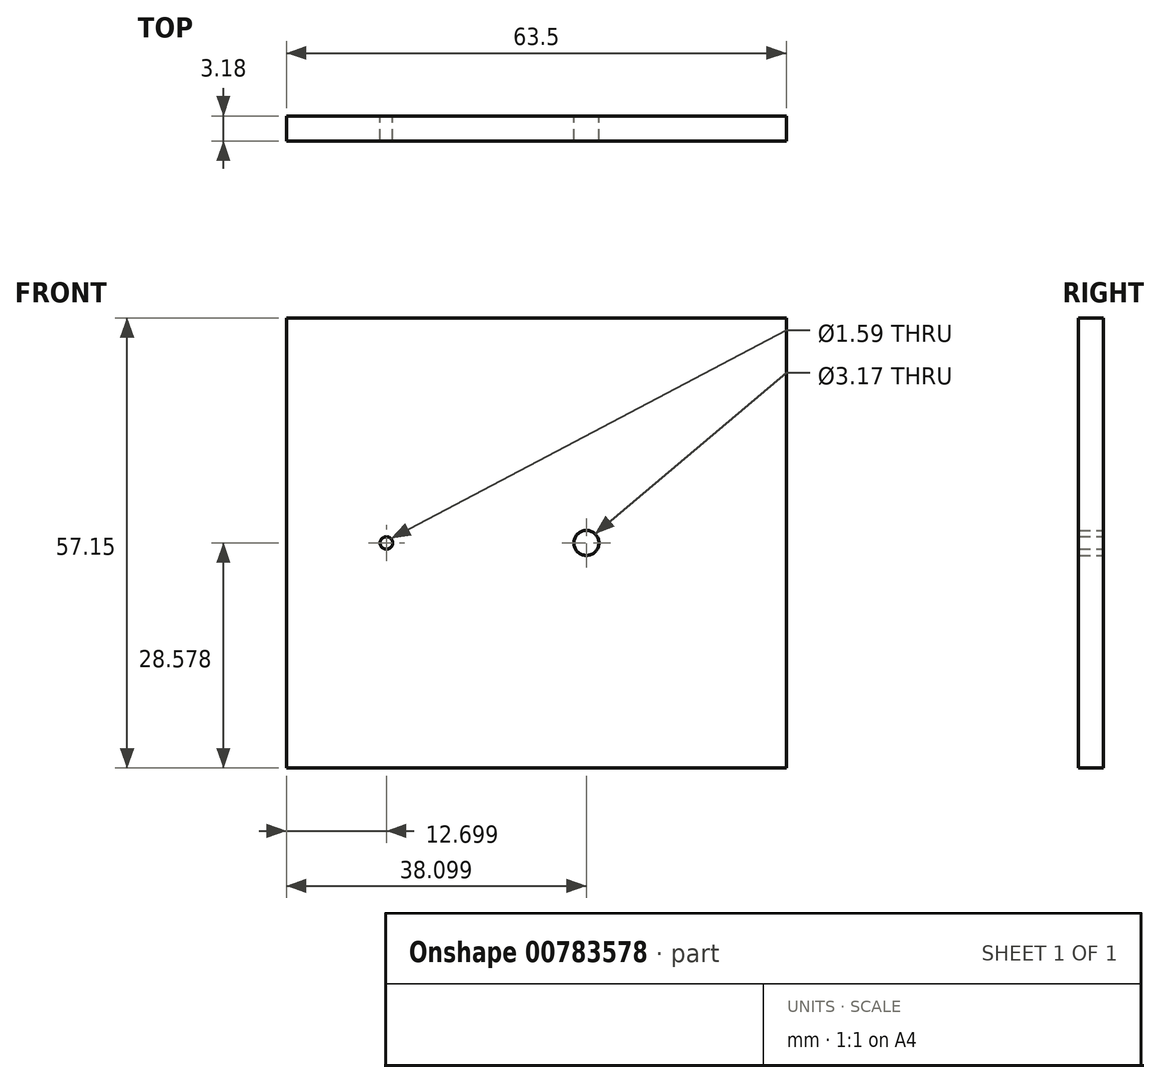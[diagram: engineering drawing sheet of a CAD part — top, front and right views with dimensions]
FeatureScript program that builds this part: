
annotation { "Feature Type Name" : "Feature", "Feature Type Description" : "" }
export const myFeature = defineFeature(function(context is Context, id is Id, definition is map)
    precondition{}
    {
        {
            var Q0;
            Q0=qCreatedBy(makeId("Front.planeOp"),FACE);
            var sketch = newSketch(context, id + "F0", { "sketchPlane" : qUnion([Q0])});
            skLineSegment(sketch, "E0.bottom", {"start": v(6.07, 29.07) * mm, "end": v(-57.43, 29.07) * mm});
            skLineSegment(sketch, "E0.top", {"start": v(6.07, -28.08) * mm, "end": v(-57.43, -28.08) * mm});
            skLineSegment(sketch, "E0.left", {"start": v(6.07, 29.07) * mm, "end": v(6.07, -28.08) * mm});
            skLineSegment(sketch, "E0.right", {"start": v(-57.43, 29.07) * mm, "end": v(-57.43, -28.08) * mm});
            skPoint(sketch, "E1", {"position": v(6.07, 0.5) * mm});
            skPoint(sketch, "E2", {"position": v(-57.43, 0.5) * mm});
            skLineSegment(sketch, "E3", {"start": v(-57.43, 0.5) * mm, "end": v(6.07, 0.5) * mm});
            skPoint(sketch, "E4", {"position": v(-44.73, 0.5) * mm});
            skCircle(sketch, "E5", {"center": v(-44.73, 0.5) * mm, "radius": 0.8 * mm});
            skPoint(sketch, "E6", {"position": v(-19.33, 0.5) * mm});
            skCircle(sketch, "E7", {"center": v(-19.33, 0.5) * mm, "radius": 1.59 * mm});
            skSolve(sketch);
        }
        {
            var Q0;
            Q0 = qSketchRegion(id + "F0", true);
            extrude(context, id + "F1", {"entities" : qUnion([Q0]), "depth" : 3.17 * mm, "offsetDistance" : 25.4 * mm});
        }
    });
